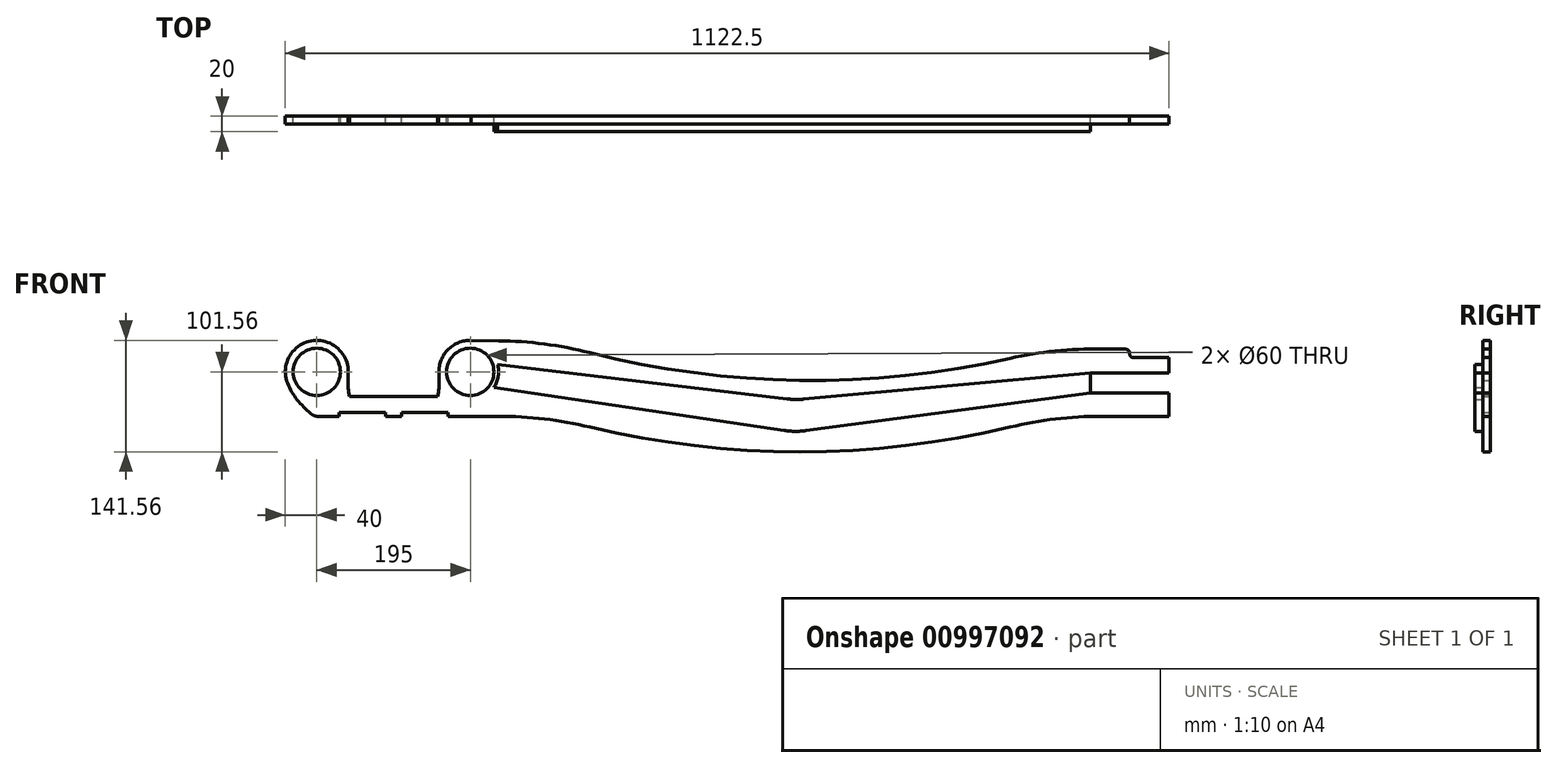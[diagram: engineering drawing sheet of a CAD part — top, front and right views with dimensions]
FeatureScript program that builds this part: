
annotation { "Feature Type Name" : "Feature", "Feature Type Description" : "" }
export const myFeature = defineFeature(function(context is Context, id is Id, definition is map)
    precondition{}
    {
        {
            var Q0;
            Q0=qCreatedBy(makeId("Front.planeOp"),FACE);
            var sketch = newSketch(context, id + "F0", { "sketchPlane" : qUnion([Q0])});
            skPoint(sketch, "E0", {"position": v(97.5, 0) * mm});
            skPoint(sketch, "E1", {"position": v(-97.5, 0) * mm});
            skCircle(sketch, "E2", {"center": v(-97.5, 0) * mm, "radius": 30 * mm});
            skCircle(sketch, "E3", {"center": v(97.5, 0) * mm, "radius": 30 * mm});
            skCircle(sketch, "E4", {"center": v(-97.5, 0) * mm, "radius": 40 * mm});
            skCircle(sketch, "E5", {"center": v(97.5, 0) * mm, "radius": 40 * mm});
            skLineSegment(sketch, "E6", {"start": v(0, 0) * mm, "end": v(0, -31.5) * mm, "construction": true});
            skLineSegment(sketch, "E7", {"start": v(0, -31.5) * mm, "end": v(56, -31.5) * mm});
            skLineSegment(sketch, "E8", {"start": v(0, -31.5) * mm, "end": v(-56, -31.5) * mm});
            skPoint(sketch, "E9", {"position": v(-57.64, -3.33) * mm});
            skArc(sketch, "E10", {"start": v(-57.64, -3.33) * mm, "mid": v(-57.82, -17.47) * mm, "end": v(-56, -31.5) * mm});
            skArc(sketch, "E11", {"start": v(56, -31.5) * mm, "mid": v(57.82, -17.47) * mm, "end": v(57.64, -3.33) * mm});
            skLineSegment(sketch, "E12", {"start": v(0, -31.5) * mm, "end": v(0, -56.5) * mm});
            skLineSegment(sketch, "E13", {"start": v(0, -56.5) * mm, "end": v(-10, -56.5) * mm});
            skLineSegment(sketch, "E14", {"start": v(0, -56.5) * mm, "end": v(10, -56.5) * mm});
            skPoint(sketch, "E15", {"position": v(-133.57, -17.3) * mm});
            skPoint(sketch, "E16", {"position": v(137.36, -3.33) * mm});
            skPoint(sketch, "E17", {"position": v(985, -3.33) * mm});
            skLineSegment(sketch, "E18", {"start": v(69, -56.5) * mm, "end": v(133.29, -56.5) * mm});
            skLineSegment(sketch, "E19", {"start": v(985, -1.75) * mm, "end": v(985, 28) * mm});
            skPoint(sketch, "E20", {"position": v(97.5, 40) * mm});
            skLineSegment(sketch, "E21", {"start": v(97.5, 40) * mm, "end": v(133.29, 39.52) * mm});
            skArc(sketch, "E22", {"start": v(-133.57, -17.3) * mm, "mid": v(-120.44, -37.81) * mm, "end": v(-102.74, -54.55) * mm});
            skPoint(sketch, "E23", {"position": v(10, -56.5) * mm});
            skLineSegment(sketch, "E24", {"start": v(10, -56.5) * mm, "end": v(10, -51.5) * mm});
            skLineSegment(sketch, "E25", {"start": v(10, -51.5) * mm, "end": v(69, -51.5) * mm});
            skLineSegment(sketch, "E26", {"start": v(69, -51.5) * mm, "end": v(69, -56.5) * mm});
            skPoint(sketch, "E27", {"position": v(-10, -56.5) * mm});
            skLineSegment(sketch, "E28", {"start": v(-10, -56.5) * mm, "end": v(-10, -51.5) * mm});
            skPoint(sketch, "E29", {"position": v(985, -14.25) * mm});
            skLineSegment(sketch, "E30", {"start": v(985, -1.75) * mm, "end": v(885, -1.75) * mm});
            skLineSegment(sketch, "E31", {"start": v(885, -1.75) * mm, "end": v(885, -26.75) * mm});
            skLineSegment(sketch, "E32", {"start": v(885, -26.75) * mm, "end": v(985, -26.75) * mm});
            skPoint(sketch, "E33", {"position": v(835, 30.03) * mm});
            skPoint(sketch, "E34", {"position": v(197.5, 38.65) * mm});
            skPoint(sketch, "E35", {"position": v(197.5, -56.5) * mm});
            skPoint(sketch, "E36", {"position": v(835, -56.5) * mm});
            skArc(sketch, "E37", {"start": v(249.15, 24.3) * mm, "mid": v(515.64, -10.72) * mm, "end": v(782.98, 17.07) * mm});
            skArc(sketch, "E38", {"start": v(249.34, -70.15) * mm, "mid": v(516.25, -101.56) * mm, "end": v(783.16, -70.15) * mm});
            skLineSegment(sketch, "E39.trimOffspring", {"start": v(899.21, 29.16) * mm, "end": v(985, 28) * mm});
            skLineSegment(sketch, "E40.trimOffspring", {"start": v(899.2, -56.5) * mm, "end": v(985, -56.5) * mm});
            skArc(sketch, "E41.filletArc", {"start": v(899.21, 29.16) * mm, "mid": v(840.74, 26.52) * mm, "end": v(782.98, 17.07) * mm});
            skArc(sketch, "E42.filletArc", {"start": v(899.2, -56.5) * mm, "mid": v(840.78, -59.93) * mm, "end": v(783.16, -70.15) * mm});
            skArc(sketch, "E43.filletArc", {"start": v(249.15, 24.3) * mm, "mid": v(191.67, 35.3) * mm, "end": v(133.29, 39.52) * mm});
            skArc(sketch, "E44.filletArc", {"start": v(249.34, -70.15) * mm, "mid": v(191.71, -59.93) * mm, "end": v(133.29, -56.5) * mm});
            skLineSegment(sketch, "E45.MirrorCS", {"start": v(-10, -51.5) * mm, "end": v(-69, -51.5) * mm});
            skLineSegment(sketch, "E46.MirrorCS", {"start": v(-69, -51.5) * mm, "end": v(-69, -56.5) * mm});
            skLineSegment(sketch, "E47.trimOffspring", {"start": v(-69, -56.5) * mm, "end": v(-96.8, -56.5) * mm});
            skLineSegment(sketch, "E48.trimOffspring", {"start": v(985, -26.75) * mm, "end": v(985, -56.5) * mm});
            skPoint(sketch, "E49", {"position": v(885, -14.25) * mm});
            skPoint(sketch, "E50.visualSharp", {"position": v(-100, -56.5) * mm});
            skArc(sketch, "E50.filletArc", {"start": v(-102.74, -54.55) * mm, "mid": v(-99.93, -56) * mm, "end": v(-96.8, -56.5) * mm});
            skSolve(sketch);
        }
        {
            var Q0;
            {var subQ0=sQuery(id+"F0.wireOp",EDGE,"E10");var subQ1=sQuery(id+"F0.wireOp",EDGE,"E4");var subQ2=makeQuery(id+"F0.imprint","INTERSECT",VERTEX,{"disambiguationData":[OD(0.0)],"derivedFrom":[subQ1,subQ0]});Q0=makeQuery(id+"F0.imprint","IMPRINT",FACE,{"disambiguationData":[TD([[makeQuery(id+"F0.imprint","IMPRINT",EDGE,{"disambiguationData":[TD([[subQ2,1.0]])],"derivedFrom":subQ1}),1.0]])]});}
            var Q1;
            {var subQ0=sQuery(id+"F0.wireOp",EDGE,"E21");var subQ1=sQuery(id+"F0.wireOp",EDGE,"E5");var subQ2=makeQuery(id+"F0.imprint","INTERSECT",VERTEX,{"disambiguationData":[OD(0.0)],"derivedFrom":[subQ1,subQ0]});Q1=makeQuery(id+"F0.imprint","IMPRINT",FACE,{"disambiguationData":[TD([[makeQuery(id+"F0.imprint","IMPRINT",EDGE,{"disambiguationData":[TD([[subQ2,1.0]])],"derivedFrom":subQ1}),1.0]])]});}
            var Q2;
            {var subQ0=sQuery(id+"F0.wireOp",EDGE,"E11");var subQ1=sQuery(id+"F0.wireOp",EDGE,"E5");var subQ2=makeQuery(id+"F0.imprint","INTERSECT",VERTEX,{"disambiguationData":[OD(0.0)],"derivedFrom":[subQ1,subQ0]});Q2=makeQuery(id+"F0.imprint","IMPRINT",FACE,{"disambiguationData":[TD([[makeQuery(id+"F0.imprint","IMPRINT",EDGE,{"disambiguationData":[TD([[subQ2,-1.0]])],"derivedFrom":subQ1}),1.0]])]});}
            var Q3;
            {var subQ1=sQuery(id+"F0.wireOp",EDGE,"E8");Q3=makeQuery(id+"F0.imprint","IMPRINT",FACE,{"disambiguationData":[TD([[makeQuery(id+"F0.imprint","IMPRINT",EDGE,{"derivedFrom":subQ1}),1.0]])]});}
            var Q4;
            Q4=makeQuery(id+"F0.imprint","IMPRINT",FACE,{"disambiguationData":[TD([[makeQuery(id+"F0.imprint","IMPRINT",EDGE,{"derivedFrom":sQuery(id+"F0.wireOp",EDGE,"E2")}),-1.0]])]});
            var Q5;
            Q5=makeQuery(id+"F0.imprint","IMPRINT",FACE,{"disambiguationData":[TD([[makeQuery(id+"F0.imprint","IMPRINT",EDGE,{"derivedFrom":sQuery(id+"F0.wireOp",EDGE,"E3")}),-1.0]])]});
            var Q6;
            {var subQ9=sQuery(id+"F0.wireOp",EDGE,"E7");Q6=makeQuery(id+"F0.imprint","IMPRINT",FACE,{"disambiguationData":[TD([[makeQuery(id+"F0.imprint","IMPRINT",EDGE,{"derivedFrom":subQ9}),-1.0]])]});}
            var Q7;
            {var subQ0=sQuery(id+"F0.wireOp",EDGE,"E38");Q7=makeQuery(id+"F0.imprint","IMPRINT",FACE,{"disambiguationData":[TD([[makeQuery(id+"F0.imprint","IMPRINT",EDGE,{"derivedFrom":subQ0}),1.0]])]});}
            extrude(context, id + "F1", {"entities" : qUnion([Q0, Q1, Q2, Q3, Q4, Q5, Q6, Q7]), "endBound" : BoundingType.SYMMETRIC, "depth" : 10 * mm, "offsetDistance" : 25 * mm});
        }
        {
            var Q0;
            {var subQ0=sQuery(id+"F0.wireOp",EDGE,"E40.trimOffspring");var subQ1=sQuery(id+"F0.wireOp",EDGE,"E39.trimOffspring");var subQ3=sQuery(id+"F0.wireOp",EDGE,"E37");var subQ4=sQuery(id+"F0.wireOp",EDGE,"E32");var subQ6=sQuery(id+"F0.wireOp",EDGE,"E31");var subQ7=sQuery(id+"F0.wireOp",EDGE,"E30");var subQ8=sQuery(id+"F0.wireOp",EDGE,"E28");var subQ9=sQuery(id+"F0.wireOp",EDGE,"E26");var subQ10=sQuery(id+"F0.wireOp",EDGE,"E25");var subQ11=sQuery(id+"F0.wireOp",EDGE,"E24");var subQ12=sQuery(id+"F0.wireOp",EDGE,"E22");var subQ13=sQuery(id+"F0.wireOp",EDGE,"E4");var subQ14=sQuery(id+"F0.wireOp",EDGE,"E3");var subQ15=sQuery(id+"F0.wireOp",EDGE,"E5");var subQ16=sQuery(id+"F0.wireOp",EDGE,"E38");var subQ17=sQuery(id+"F0.wireOp",EDGE,"E2");var subQ18=sQuery(id+"F0.wireOp",EDGE,"E8");var subQ19=sQuery(id+"F0.wireOp",EDGE,"E7");var subQ20=sQuery(id+"F0.wireOp",EDGE,"E10");var subQ21=sQuery(id+"F0.wireOp",EDGE,"E11");var subQ22=sQuery(id+"F0.wireOp",EDGE,"E14");var subQ23=sQuery(id+"F0.wireOp",EDGE,"E13");var subQ24=sQuery(id+"F0.wireOp",EDGE,"E18");var subQ25=sQuery(id+"F0.wireOp",EDGE,"E21");var subQ26=sQuery(id+"F0.wireOp",EDGE,"E41.filletArc");var subQ27=sQuery(id+"F0.wireOp",EDGE,"GA7PutSn-Nesw-1cXz-VhA8-feTON509f17w");var subQ28=sQuery(id+"F0.wireOp",EDGE,"E42.filletArc");var subQ29=sQuery(id+"F0.wireOp",EDGE,"E43.filletArc");var subQ30=sQuery(id+"F0.wireOp",EDGE,"E44.filletArc");Q0=makeQuery(id+"FWcALs99ztQsV3U_4.opBoolean","SPLIT",FACE,{"disambiguationData":[TD([makeQuery(id+"F1.opExtrude","SWEPT_FACE",FACE,{"disambiguationData":[OSD([subQ17])]})])],"derivedFrom":makeQuery(id+"F1.opExtrude","CAP_FACE",FACE,{"disambiguationData":[OSD([subQ17,subQ14,subQ13,subQ15,subQ19,subQ18,subQ20,subQ21,subQ23,subQ22,subQ24,sQuery(id+"F0.wireOp",EDGE,"qz4P9ecO-jNwn-Qn5e-R75e-66BUEQRMrbO0"),sQuery(id+"F0.wireOp",EDGE,"E19"),subQ25,subQ12,subQ11,subQ10,subQ9,subQ8,subQ7,subQ6,subQ4,subQ3,subQ16,subQ1,subQ0,subQ26,subQ28,subQ29,subQ30,subQ27])],"isStart":false})});}
            var sketch = newSketch(context, id + "F2", { "sketchPlane" : qUnion([Q0])});
            skLineSegment(sketch, "E51", {"start": v(885, -1.75) * mm, "end": v(520.47, -34.7) * mm});
            skLineSegment(sketch, "E52", {"start": v(499.56, -34.39) * mm, "end": v(132.18, 9.66) * mm});
            skLineSegment(sketch, "E53", {"start": v(127.56, -19.81) * mm, "end": v(496.1, -74.48) * mm});
            skLineSegment(sketch, "E54", {"start": v(523.93, -74.7) * mm, "end": v(885, -26.75) * mm});
            skLineSegment(sketch, "E55", {"start": v(885, -1.75) * mm, "end": v(885, -26.75) * mm});
            skPoint(sketch, "E56.visualSharp", {"position": v(510, -35.64) * mm});
            skArc(sketch, "E56.filletArc", {"start": v(499.56, -34.39) * mm, "mid": v(510, -35.09) * mm, "end": v(520.47, -34.7) * mm});
            skPoint(sketch, "E57.visualSharp", {"position": v(510, -76.54) * mm});
            skArc(sketch, "E57.filletArc", {"start": v(496.1, -74.48) * mm, "mid": v(510, -75.56) * mm, "end": v(523.93, -74.7) * mm});
            skArc(sketch, "E58", {"start": v(127.56, -19.81) * mm, "mid": v(133.07, -5.58) * mm, "end": v(132.18, 9.66) * mm});
            skSolve(sketch);
        }
        {
            var Q0;
            Q0=qSketchRegion(id+"F2",true);
            extrude(context, id + "F3", {"entities" : qUnion([Q0]), "depth" : 10 * mm, "offsetDistance" : 25 * mm});
        }
        {
            var Q0;
            Q0=makeQuery(id+"F1.opExtrude","CAP_FACE",FACE,{"disambiguationData":[OSD([sQuery(id+"F0.wireOp",EDGE,"E2"),sQuery(id+"F0.wireOp",EDGE,"E3"),sQuery(id+"F0.wireOp",EDGE,"E4"),sQuery(id+"F0.wireOp",EDGE,"E5"),sQuery(id+"F0.wireOp",EDGE,"E7"),sQuery(id+"F0.wireOp",EDGE,"E8"),sQuery(id+"F0.wireOp",EDGE,"E10"),sQuery(id+"F0.wireOp",EDGE,"E11"),sQuery(id+"F0.wireOp",EDGE,"E13"),sQuery(id+"F0.wireOp",EDGE,"E14"),sQuery(id+"F0.wireOp",EDGE,"E18"),sQuery(id+"F0.wireOp",EDGE,"E19"),sQuery(id+"F0.wireOp",EDGE,"E21"),sQuery(id+"F0.wireOp",EDGE,"E22"),sQuery(id+"F0.wireOp",EDGE,"E24"),sQuery(id+"F0.wireOp",EDGE,"E25"),sQuery(id+"F0.wireOp",EDGE,"E26"),sQuery(id+"F0.wireOp",EDGE,"E30"),sQuery(id+"F0.wireOp",EDGE,"E31"),sQuery(id+"F0.wireOp",EDGE,"E32"),sQuery(id+"F0.wireOp",EDGE,"E37"),sQuery(id+"F0.wireOp",EDGE,"E38"),sQuery(id+"F0.wireOp",EDGE,"E39.trimOffspring"),sQuery(id+"F0.wireOp",EDGE,"E40.trimOffspring"),sQuery(id+"F0.wireOp",EDGE,"E41.filletArc"),sQuery(id+"F0.wireOp",EDGE,"E42.filletArc"),sQuery(id+"F0.wireOp",EDGE,"E43.filletArc"),sQuery(id+"F0.wireOp",EDGE,"E44.filletArc"),sQuery(id+"F0.wireOp",EDGE,"E28"),sQuery(id+"F0.wireOp",EDGE,"E45.MirrorCS"),sQuery(id+"F0.wireOp",EDGE,"E46.MirrorCS"),sQuery(id+"F0.wireOp",EDGE,"E47.trimOffspring"),sQuery(id+"F0.wireOp",EDGE,"E48.trimOffspring"),sQuery(id+"F0.wireOp",EDGE,"E50.filletArc")])],"isStart":false});
            var sketch = newSketch(context, id + "F4", { "sketchPlane" : qUnion([Q0])});
            skLineSegment(sketch, "E59.bottom", {"start": v(985, 18) * mm, "end": v(935, 18) * mm});
            skLineSegment(sketch, "E59.top", {"start": v(985, 70.28) * mm, "end": v(935, 70.28) * mm});
            skLineSegment(sketch, "E59.left", {"start": v(985, 18) * mm, "end": v(985, 70.28) * mm});
            skLineSegment(sketch, "E59.right", {"start": v(935, 18) * mm, "end": v(935, 70.28) * mm});
            skPoint(sketch, "E60", {"position": v(985, 28) * mm});
            skSolve(sketch);
        }
        {
            var Q0;
            Q0 = qSketchRegion(id + "F4", true);
            extrude(context, id + "F5", {"entities" : qUnion([Q0]), "operationType" : NewBodyOperationType.REMOVE, "oppositeDirection" : true, "depth" : 25 * mm, "offsetDistance" : 25 * mm});
        }
        {
            var Q0;
            Q0=makeQuery(id+"F5.boolean.opBoolean","COPY",EDGE,{"derivedFrom":makeQuery(id+"F5.opExtrude","SWEPT_EDGE",EDGE,{"disambiguationData":[OSD([sQuery(id+"F4.wireOp",EDGE,"E59.bottom"),sQuery(id+"F4.wireOp",EDGE,"E59.right")])]})});
            var Q1;
            Q1=makeQuery(id+"F5.boolean.opBoolean","INTERSECT",EDGE,{"derivedFrom":[makeQuery(id+"F1.opExtrude","SWEPT_FACE",FACE,{"disambiguationData":[OSD([sQuery(id+"F0.wireOp",EDGE,"E39.trimOffspring")])]}),makeQuery(id+"F5.opExtrude","SWEPT_FACE",FACE,{"disambiguationData":[OSD([sQuery(id+"F4.wireOp",EDGE,"E59.right")])]})]});
            fillet(context, id + "F6", {"entities" : qUnion([Q0, Q1]), "radius" : 5 * mm, "tangentPropagation" : true, "allowEdgeOverflow" : false});
        }
    });
